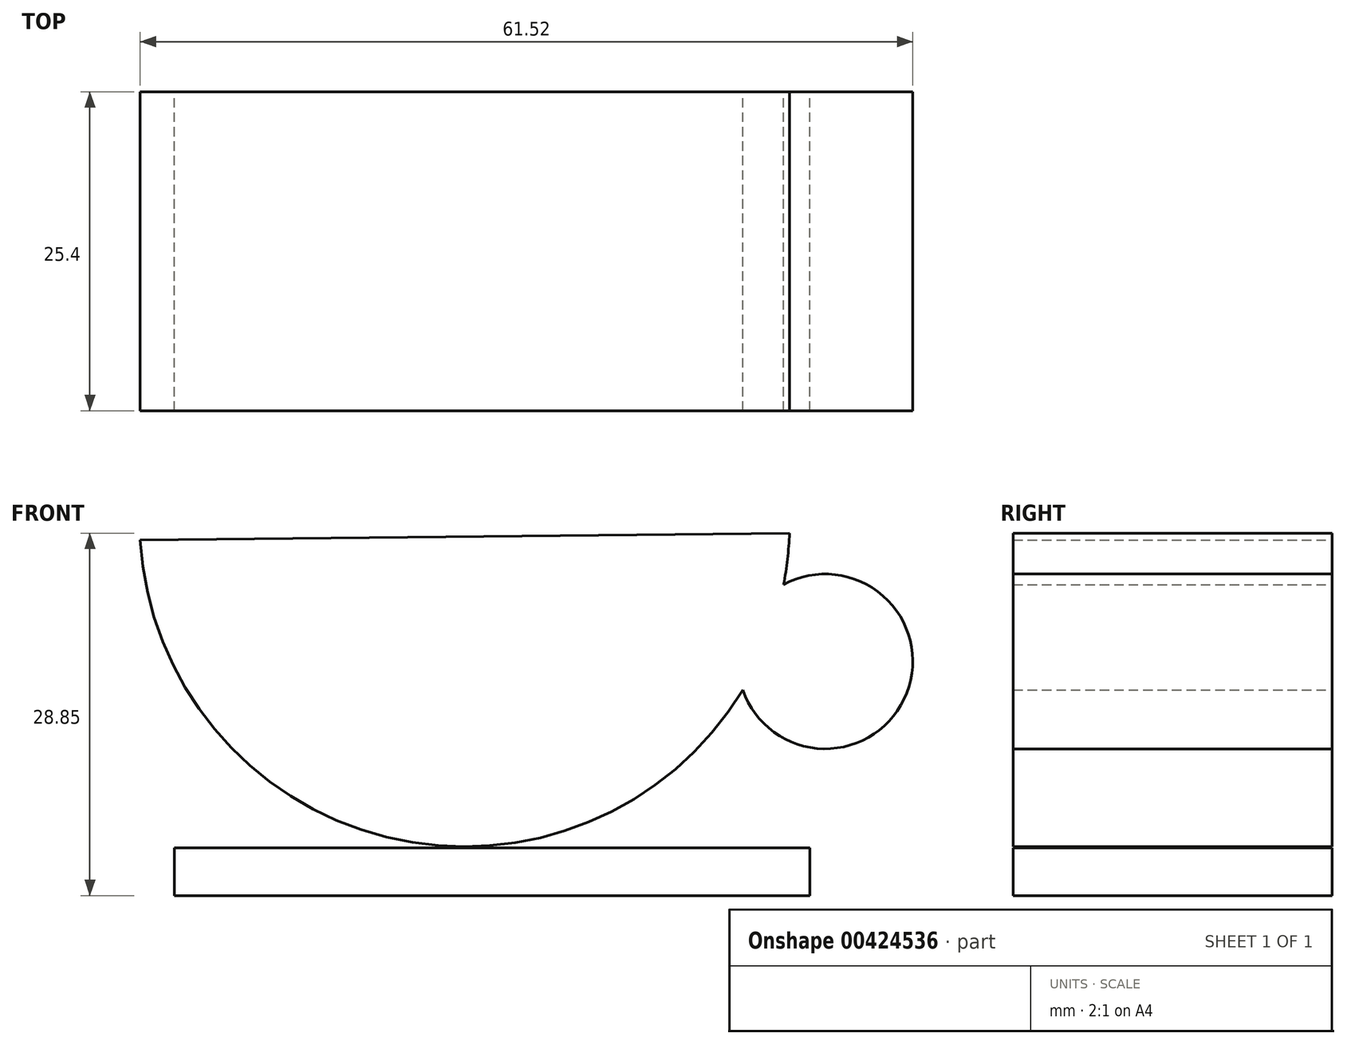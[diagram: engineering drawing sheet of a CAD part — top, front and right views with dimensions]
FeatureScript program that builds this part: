
annotation { "Feature Type Name" : "Feature", "Feature Type Description" : "" }
export const myFeature = defineFeature(function(context is Context, id is Id, definition is map)
    precondition{}
    {
        {
            var Q0;
            Q0=qCreatedBy(makeId("Front.planeOp"),FACE);
            var sketch = newSketch(context, id + "F0", { "sketchPlane" : qUnion([Q0])});
            skPoint(sketch, "E0", {"position": v(20.14, 24.5) * mm});
            skLineSegment(sketch, "E1", {"start": v(-25.3, -9.8) * mm, "end": v(25.3, -9.8) * mm});
            skLineSegment(sketch, "E2", {"start": v(-25.3, -9.8) * mm, "end": v(-25.3, -13.6) * mm});
            skLineSegment(sketch, "E3", {"start": v(-25.3, -13.6) * mm, "end": v(25.3, -13.6) * mm});
            skLineSegment(sketch, "E4", {"start": v(25.3, -13.6) * mm, "end": v(25.3, -9.8) * mm});
            skPoint(sketch, "E5.center.orphan", {"position": v(17.86, 0) * mm});
            skPoint(sketch, "E6.center.orphan", {"position": v(14.7, 0) * mm});
            skArc(sketch, "E7", {"start": v(-28.03, 14.7) * mm, "mid": v(-1.92, -9.71) * mm, "end": v(23.68, 15.24) * mm});
            skLineSegment(sketch, "E8", {"start": v(-28.03, 14.7) * mm, "end": v(23.68, 15.24) * mm});
            skArc(sketch, "E9", {"start": v(19.95, 2.76) * mm, "mid": v(33.01, 2.52) * mm, "end": v(23.2, 11.15) * mm});
            skSolve(sketch);
        }
        {
            var Q0;
            {var subQ0=sQuery(id+"F0.wireOp",EDGE,"E8");Q0=makeQuery(id+"F0.imprint","IMPRINT",FACE,{"disambiguationData":[TD([[makeQuery(id+"F0.imprint","IMPRINT",EDGE,{"derivedFrom":subQ0}),-1.0]])]});}
            var Q1;
            {var subQ0=sQuery(id+"F0.wireOp",EDGE,"E9");Q1=makeQuery(id+"F0.imprint","IMPRINT",FACE,{"disambiguationData":[TD([[makeQuery(id+"F0.imprint","IMPRINT",EDGE,{"derivedFrom":subQ0}),1.0]])]});}
            var Q2;
            Q2=makeQuery(id+"F0.imprint","IMPRINT",FACE,{"disambiguationData":[TD([[makeQuery(id+"F0.imprint","IMPRINT",EDGE,{"derivedFrom":sQuery(id+"F0.wireOp",EDGE,"E1")}),-1.0]])]});
            extrude(context, id + "F1", {"entities" : qUnion([Q0, Q1, Q2]), "depth" : 25.4 * mm});
        }
    });
